# Revit family: Urinal-Flush_Actuator_Sensor-KOHLER-Summon-K-29181T_1
name_source: partatom
category: Plumbing Fixtures
units: mm (PartAtom-declared; Revit-internal decimal feet)

## family parameters
Cut with Voids When Loaded = No
Host = Face
OmniClass Number = 23.31.25.00
OmniClass Title = Toilet and Bath Specialties
Part Type = Normal
Room Calculation Point = No
Round Connector Dimension = Use Diameter
Shared = No

## types (4) — shared parameters
ADA Compliant = No
Apparent Load = 0 VA
Assembly Code = D2020
CW Connection = Yes
Cold Water Inlet = Cold Water Inlet
Cold Water Outlet = Cold Water Outlet
Date Modified = 08/08/2022
Default Elevation = 36"
Electrical Connector = Yes
Electrical Note = One Dedicated Circuit Required
Finish = Kohler-Glass-7-Black_Black
Flow Rate = 0 GPM
HW Connection = No
Height = 4 15/16"
Hot Water Inlet = Hot Water Inlet
Length = 3/16"
Manufacturer = Kohler Co.
Master Format 2014 = 22 41 39
Master Format 2014 Name = Residential Faucets, Supplies, and Trim
Material = Glass
Pressure = 80.00 psi
Product Name = Summon
URL = http://www.kohler.com.cn
Vent Connection = No
Voltage = 220 V
Waste Connection = No
Waste Water Outlet = Waste Water Outlet
WaterSense Certified = No
Width = 4 15/16"

## per-type parameters (varying)
| type | Description | Flush Rate- LPF | Model | Type |
| 2.5 LPF, 7-Black | Urinal Sensor 2.5 LPF | 2.5 LPF | K-29181T-2-7 | 1 |
| 1.0 LPF, 7-Black | Urinal Sensor 1.0 LPF | 1.0 LPF | K-29181T-2W-7 | 2 |
| 0.5 LPF, 7-Black | Urinal Sensor 0.5 LPF | 0.5 LPF | K-29181T-2Y-7 | 3 |
| 0.5 LPF-IOT, 7-Black | Urinal Sensor 0.5 LPF- Internet Of Things | 0.5 LPF | K-29181T-2YX-7 | 4 |

## geometry (parser evidence)
native form markers: Sweep x7
no freeform markers — native parametric forms only
